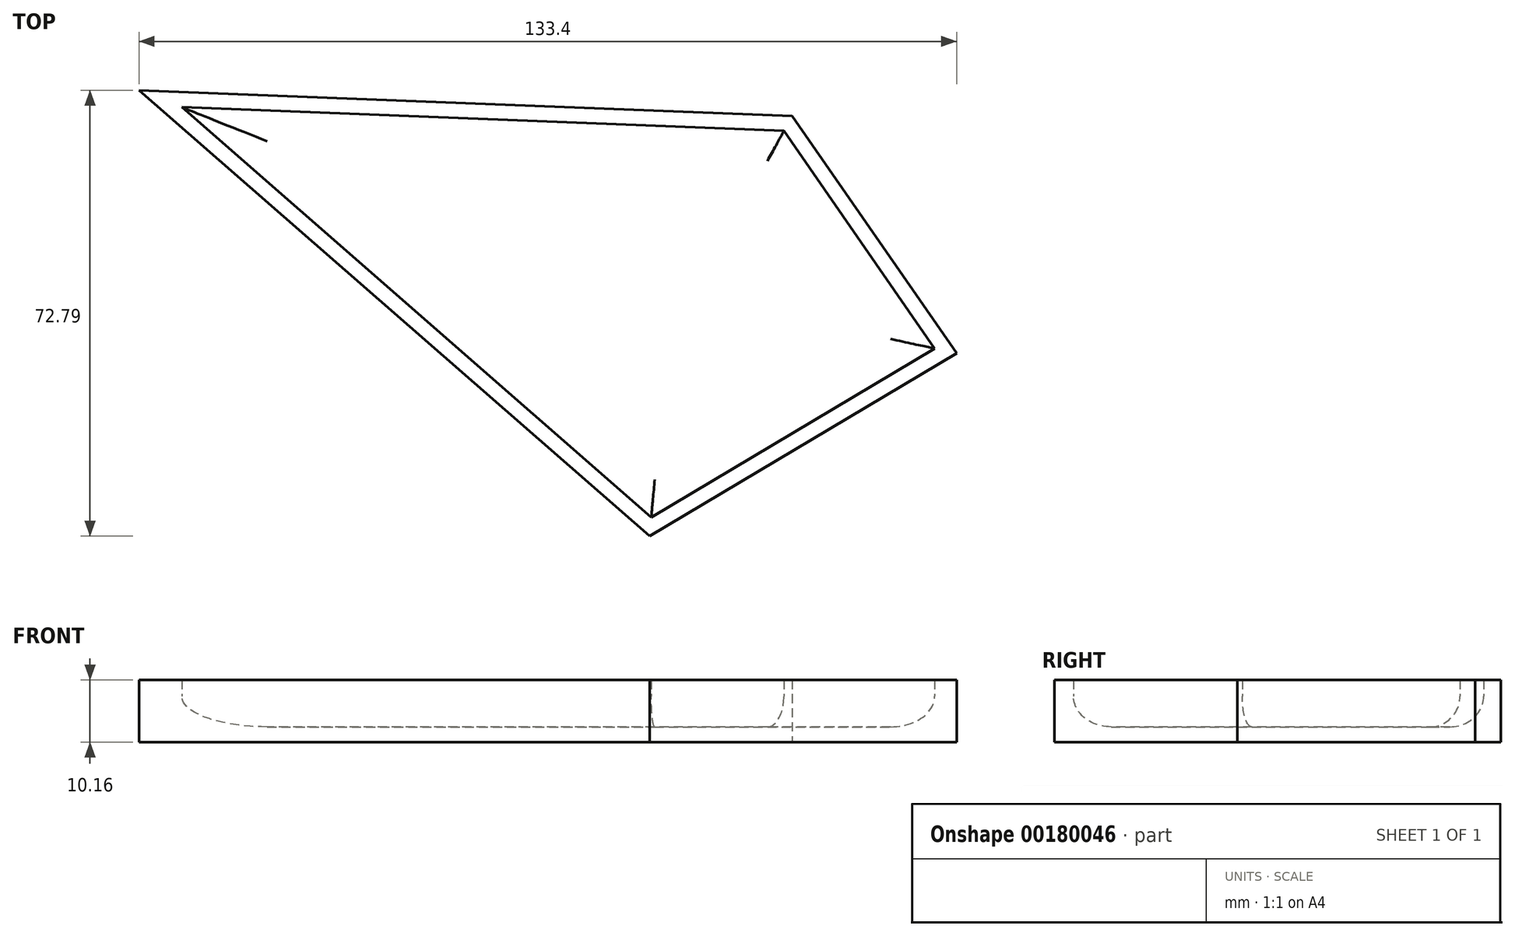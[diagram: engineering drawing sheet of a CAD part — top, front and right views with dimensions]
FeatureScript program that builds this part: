
annotation { "Feature Type Name" : "Feature", "Feature Type Description" : "" }
export const myFeature = defineFeature(function(context is Context, id is Id, definition is map)
    precondition{}
    {
        {
            var Q0;
            Q0=qCreatedBy(makeId("Top.planeOp"),FACE);
            var sketch = newSketch(context, id + "F0", { "sketchPlane" : qUnion([Q0])});
            skLineSegment(sketch, "E0", {"start": v(-101.88, 11.49) * mm, "end": v(-18.57, -61.3) * mm});
            skLineSegment(sketch, "E1", {"start": v(-18.57, -61.3) * mm, "end": v(31.52, -31.46) * mm});
            skLineSegment(sketch, "E2", {"start": v(31.52, -31.46) * mm, "end": v(4.7, 7.29) * mm});
            skLineSegment(sketch, "E3", {"start": v(4.7, 7.29) * mm, "end": v(-101.88, 11.49) * mm});
            skSolve(sketch);
        }
        {
            var Q0;
            Q0=makeQuery(id+"F0.imprint","IMPRINT",FACE,{"disambiguationData":[TD([[makeQuery(id+"F0.imprint","IMPRINT",EDGE,{"derivedFrom":sQuery(id+"F0.wireOp",EDGE,"E0")}),1.0]])]});
            extrude(context, id + "F1", {"entities" : qUnion([Q0]), "depth" : 10.16 * mm});
        }
        {
            var Q0;
            Q0=makeQuery(id+"F1.opExtrude","CAP_FACE",FACE,{"disambiguationData":[OSD([sQuery(id+"F0.wireOp",EDGE,"E0"),sQuery(id+"F0.wireOp",EDGE,"E1"),sQuery(id+"F0.wireOp",EDGE,"E2"),sQuery(id+"F0.wireOp",EDGE,"E3")])],"isStart":false});
            shell(context, id + "F2", {"entities" : qUnion([Q0]), "thickness" : 2.5 * mm});
        }
        {
            var Q0;
            Q0=makeQuery(id+"F2.opShell","OFFSET_FACE",FACE,{"disambiguationData":[OSD([sQuery(id+"F0.wireOp",EDGE,"E0"),sQuery(id+"F0.wireOp",EDGE,"E1"),sQuery(id+"F0.wireOp",EDGE,"E2"),sQuery(id+"F0.wireOp",EDGE,"E3")])]});
            fillet(context, id + "F3", {"entities" : qUnion([Q0]), "radius" : 5 * mm, "tangentPropagation" : true, "allowEdgeOverflow" : false});
        }
    });
